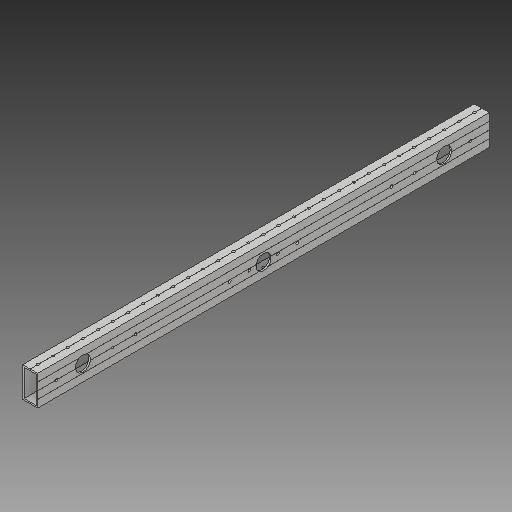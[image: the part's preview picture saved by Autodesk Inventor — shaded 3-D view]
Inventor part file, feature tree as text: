
AUTODESK INVENTOR PART (.ipt)
format: ipt  version: 2017 (Build 210142000, 142)  size: 653,824 bytes
history: native  units: in
note: dims shown in document units (in); Inventor stores cm internally (conversion verified against a paired STEP export)
features: other x3, sketch x2
ambient origin geometry x8: Origin, YZ Plane, XZ Plane, XY Plane, X Axis, Y Axis, Z Axis, Center Point
bodies: Solid1 (feature_tree)
feature tree (5):
  other  "2898-17-P-0101.ipt"
  other  "Solid1::2898-17-P-0101.ipt"
  other  "TaggingFeature1"
  sketch  "Sketch1"  dims[d0=0.3937in]
  sketch  "Sketch2"
